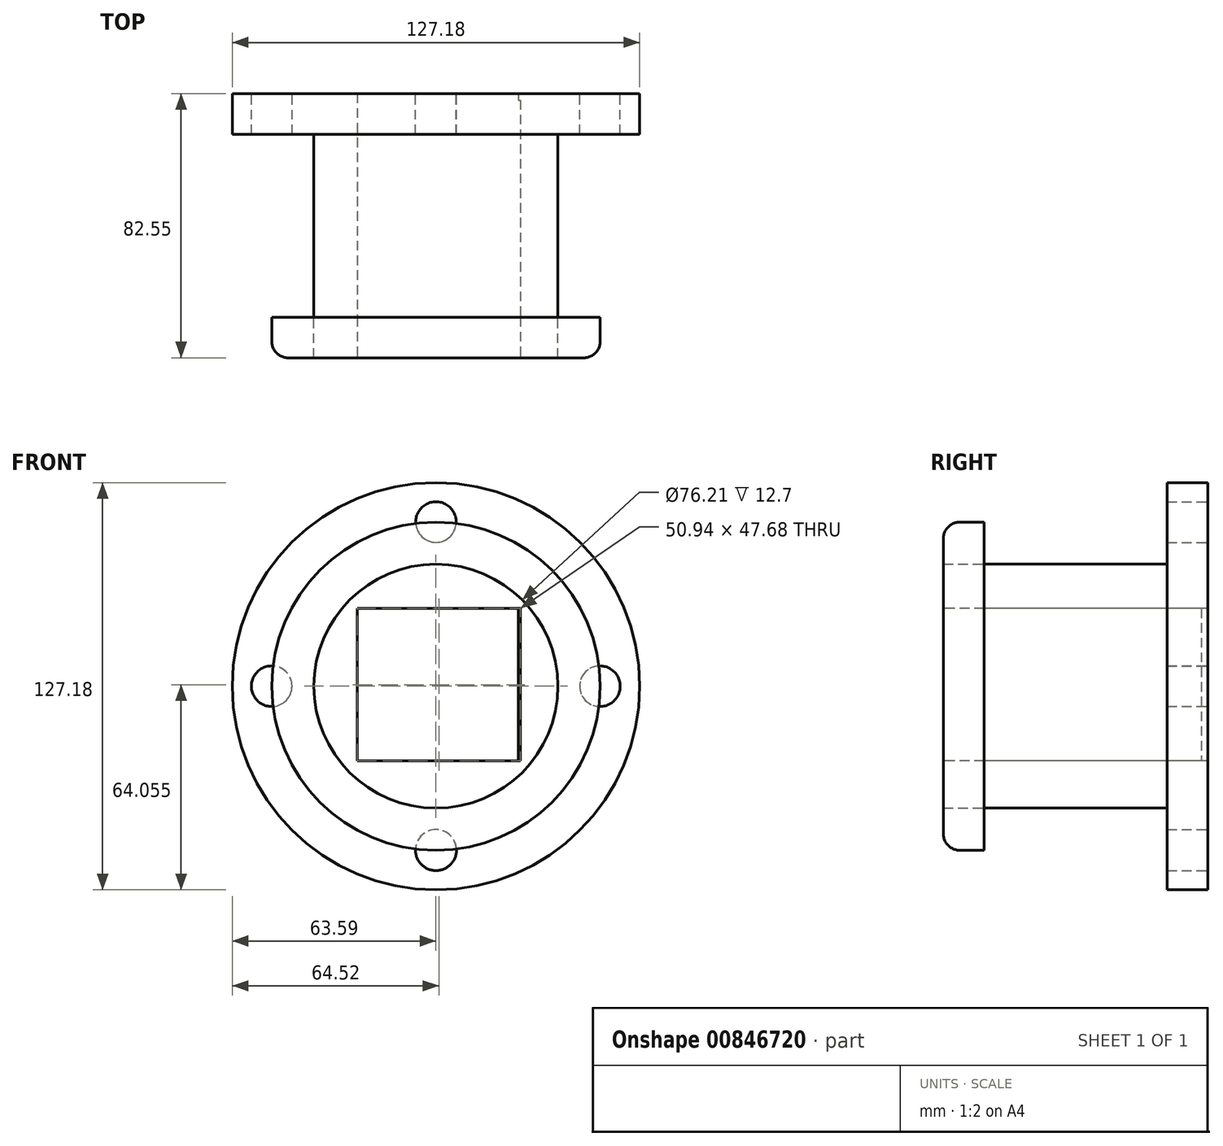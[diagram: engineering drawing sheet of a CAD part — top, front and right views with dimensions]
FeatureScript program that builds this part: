
annotation { "Feature Type Name" : "Feature", "Feature Type Description" : "" }
export const myFeature = defineFeature(function(context is Context, id is Id, definition is map)
    precondition{}
    {
        {
            var Q0;
            Q0=qCreatedBy(makeId("Front.planeOp"),FACE);
            var sketch = newSketch(context, id + "F0", { "sketchPlane" : qUnion([Q0])});
            skCircle(sketch, "E0", {"center": v(0, 0) * mm, "radius": 63.59 * mm});
            skCircle(sketch, "E1", {"center": v(-51.29, 0) * mm, "radius": 6.35 * mm});
            skCircle(sketch, "E2", {"center": v(0, 51.29) * mm, "radius": 6.35 * mm});
            skCircle(sketch, "E3", {"center": v(0, 0) * mm, "radius": 51.2 * mm});
            skPoint(sketch, "E4.center.orphan", {"position": v(0, -48.26) * mm});
            skPoint(sketch, "E5.center.orphan", {"position": v(46.87, 0) * mm});
            skCircle(sketch, "E6", {"center": v(0, -51.2) * mm, "radius": 6.4 * mm});
            skCircle(sketch, "E7", {"center": v(51.2, 0) * mm, "radius": 6.34 * mm});
            skSolve(sketch);
        }
        {
            var Q0;
            Q0=makeQuery(id+"F0.imprint","IMPRINT",FACE,{"disambiguationData":[TD([[makeQuery(id+"F0.imprint","IMPRINT",EDGE,{"derivedFrom":sQuery(id+"F0.wireOp",EDGE,"E0")}),1.0]])]});
            var Q1;
            {var subQ0=sQuery(id+"F0.wireOp",EDGE,"E3");var subQ6=sQuery(id+"F0.wireOp",EDGE,"E1");var subQ7=makeQuery(id+"F0.imprint","INTERSECT",VERTEX,{"disambiguationData":[OD(0.0)],"derivedFrom":[subQ6,subQ0]});Q1=makeQuery(id+"F0.imprint","IMPRINT",FACE,{"disambiguationData":[TD([[makeQuery(id+"F0.imprint","IMPRINT",EDGE,{"disambiguationData":[TD([[subQ7,1.0]])],"derivedFrom":subQ6}),-1.0]])]});}
            extrude(context, id + "F1", {"entities" : qUnion([Q0, Q1]), "depth" : 12.7 * mm, "offsetDistance" : 25.4 * mm});
        }
        {
            var Q0;
            Q0=makeQuery(id+"F1.opExtrude","CAP_FACE",FACE,{"disambiguationData":[OSD([sQuery(id+"F0.wireOp",EDGE,"E0"),sQuery(id+"F0.wireOp",EDGE,"E1"),sQuery(id+"F0.wireOp",EDGE,"E2"),sQuery(id+"F0.wireOp",EDGE,"E6"),sQuery(id+"F0.wireOp",EDGE,"E7")])],"isStart":false});
            var sketch = newSketch(context, id + "F2", { "sketchPlane" : qUnion([Q0])});
            skCircle(sketch, "E8", {"center": v(0, 0) * mm, "radius": 38.1 * mm});
            skSolve(sketch);
        }
        {
            var Q0;
            Q0=makeQuery(id+"F2.imprint","IMPRINT",FACE,{"disambiguationData":[TD([[makeQuery(id+"F2.imprint","IMPRINT",EDGE,{"derivedFrom":sQuery(id+"F2.wireOp",EDGE,"E8")}),1.0]])]});
            extrude(context, id + "F3", {"entities" : qUnion([Q0]), "operationType" : NewBodyOperationType.ADD, "depth" : 57.15 * mm, "offsetDistance" : 25.4 * mm});
        }
        {
            var Q0;
            Q0=makeQuery(id+"F3.opExtrude","CAP_FACE",FACE,{"disambiguationData":[OSD([sQuery(id+"F2.wireOp",EDGE,"E8")])],"isStart":false});
            var sketch = newSketch(context, id + "F4", { "sketchPlane" : qUnion([Q0])});
            skCircle(sketch, "E9", {"center": v(0, 0) * mm, "radius": 51.25 * mm});
            skSolve(sketch);
        }
        {
            var Q0;
            Q0=makeQuery(id+"F4.imprint","IMPRINT",FACE,{"disambiguationData":[TD([[makeQuery(id+"F4.imprint","IMPRINT",EDGE,{"derivedFrom":sQuery(id+"F4.wireOp",EDGE,"E9")}),1.0]])]});
            extrude(context, id + "F5", {"entities" : qUnion([Q0]), "depth" : 12.7 * mm, "offsetDistance" : 25.4 * mm});
        }
        {
            var Q0;
            Q0=makeQuery(id+"F3.opExtrude","CAP_FACE",FACE,{"disambiguationData":[OSD([sQuery(id+"F2.wireOp",EDGE,"E8")])],"isStart":false});
            extrude(context, id + "F6", {"entities" : qUnion([Q0]), "depth" : 12.7 * mm, "offsetDistance" : 25.4 * mm});
        }
        {
            var Q0;
            Q0=makeQuery(id+"F6.opExtrude","CAP_FACE",FACE,{"disambiguationData":[OSD([sQuery(id+"F2.wireOp",EDGE,"E8")])],"isStart":false});
            var sketch = newSketch(context, id + "F7", { "sketchPlane" : qUnion([Q0])});
            skLineSegment(sketch, "E10.bottom", {"start": v(-24.54, 24.3) * mm, "end": v(26.4, 24.3) * mm});
            skLineSegment(sketch, "E10.top", {"start": v(-24.54, -23.38) * mm, "end": v(26.4, -23.38) * mm});
            skLineSegment(sketch, "E10.left", {"start": v(-24.54, 24.3) * mm, "end": v(-24.54, -23.38) * mm});
            skLineSegment(sketch, "E10.right", {"start": v(26.4, 24.3) * mm, "end": v(26.4, -23.38) * mm});
            skSolve(sketch);
        }
        {
            var Q0;
            Q0 = qSketchRegion(id + "F7", true);
            extrude(context, id + "F8", {"entities" : qUnion([Q0]), "operationType" : NewBodyOperationType.REMOVE, "oppositeDirection" : true, "depth" : 80.52 * mm, "offsetDistance" : 25.4 * mm});
        }
        {
            var Q0;
            Q0=makeQuery(id+"F3.opExtrude","CAP_FACE",FACE,{"disambiguationData":[OSD([sQuery(id+"F2.wireOp",EDGE,"E8")])],"isStart":false});
            var sketch = newSketch(context, id + "F9", { "sketchPlane" : qUnion([Q0])});
            skLineSegment(sketch, "E11.bottom", {"start": v(-24.54, 24.3) * mm, "end": v(25.7, 24.3) * mm});
            skLineSegment(sketch, "E11.top", {"start": v(-24.54, -23.38) * mm, "end": v(25.7, -23.38) * mm});
            skLineSegment(sketch, "E11.left", {"start": v(-24.54, 24.3) * mm, "end": v(-24.54, -23.38) * mm});
            skLineSegment(sketch, "E11.right", {"start": v(25.7, 24.3) * mm, "end": v(25.7, -23.38) * mm});
            skSolve(sketch);
        }
        {
            var Q0;
            Q0=makeQuery(id+"F9.imprint","IMPRINT",FACE,{"disambiguationData":[TD([[makeQuery(id+"F9.imprint","IMPRINT",EDGE,{"derivedFrom":sQuery(id+"F9.wireOp",EDGE,"E11.bottom")}),-1.0]])]});
            extrude(context, id + "F10", {"entities" : qUnion([Q0]), "operationType" : NewBodyOperationType.REMOVE, "oppositeDirection" : true, "depth" : 76.2 * mm, "offsetDistance" : 25.4 * mm});
        }
        {
            var Q0;
            Q0=makeQuery(id+"F5.opExtrude","CAP_EDGE",EDGE,{"disambiguationData":[OSD([sQuery(id+"F4.wireOp",EDGE,"E9")])],"isStart":false});
            fillet(context, id + "F11", {"entities" : qUnion([Q0]), "radius" : 5.08 * mm, "tangentPropagation" : true, "allowEdgeOverflow" : false});
        }
    });
